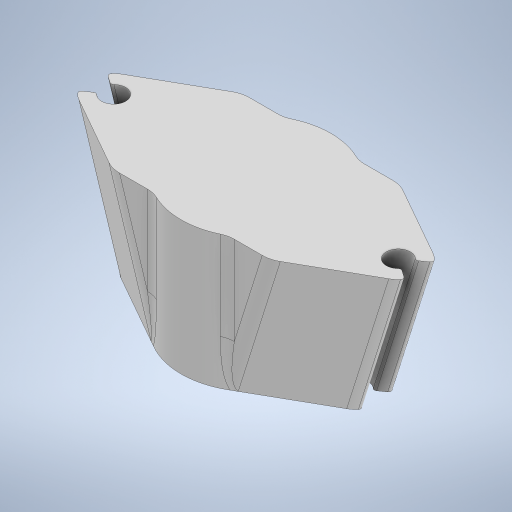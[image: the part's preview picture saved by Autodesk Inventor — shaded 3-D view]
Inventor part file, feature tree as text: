
AUTODESK INVENTOR PART (.ipt)
format: ipt  version: 2023 (Build 270158000, 158)  size: 406,528 bytes
history: native  units: in
note: dims shown in document units (in); Inventor stores cm internally (conversion verified against a paired STEP export)
features: sketch x5, extrude x4, sweep x2, fillet x2, projected_geometry x1
ambient origin geometry x8: Origin, YZ Plane, XZ Plane, XY Plane, X Axis, Y Axis, Z Axis, Center Point
bodies: Body1 (feature_tree)
feature tree (14):
  sketch  "Sketch5"  dims[d48=0.56in d54=0.5in]
  sketch  "Sketch1"  dims[d21=0.2405in d22=0.2405in]
  sweep  "Sweep1"
  sweep  "Sweep2"
  extrude  "Extrusion4"  Depth=0.2405in
  extrude  "Extrusion5"  TaperAngle=0.0deg  [1 undecoded]
  fillet  "Fillet3"  [1 undecoded]
  fillet  "Fillet4"  Radius=0.5in
  extrude  "Extrusion6"  Depth=0.1in
  extrude  "Extrusion7"  Depth=0.1in TaperAngle=0.0deg
  sketch  "Sketch7"  dims[d55=0.1202in d56=0.2405in]
  projected_geometry  "Projected Loop4"
  sketch  "Sketch8"  dims[d57=0.1202in d58=0.0in d59=0.0in d60=0.0in d61=0.0in d64=0.5in]
  sketch  "Sketch9"  dims[d65=0.0in d66=0.41in d67=0.45in d68=0.0in d69=0.01in d70=0.1in d71=0.04in d72=0.0in d73=0.04in d74=0.0in d15=0.0in d16=0.0in d17=0.0in d18=0.0in]
note: 2 required parameter values undecoded (feature->parameter linkage not recoverable at this tier; creation-order binding heuristic only, values carry confidence <= 0.55)
